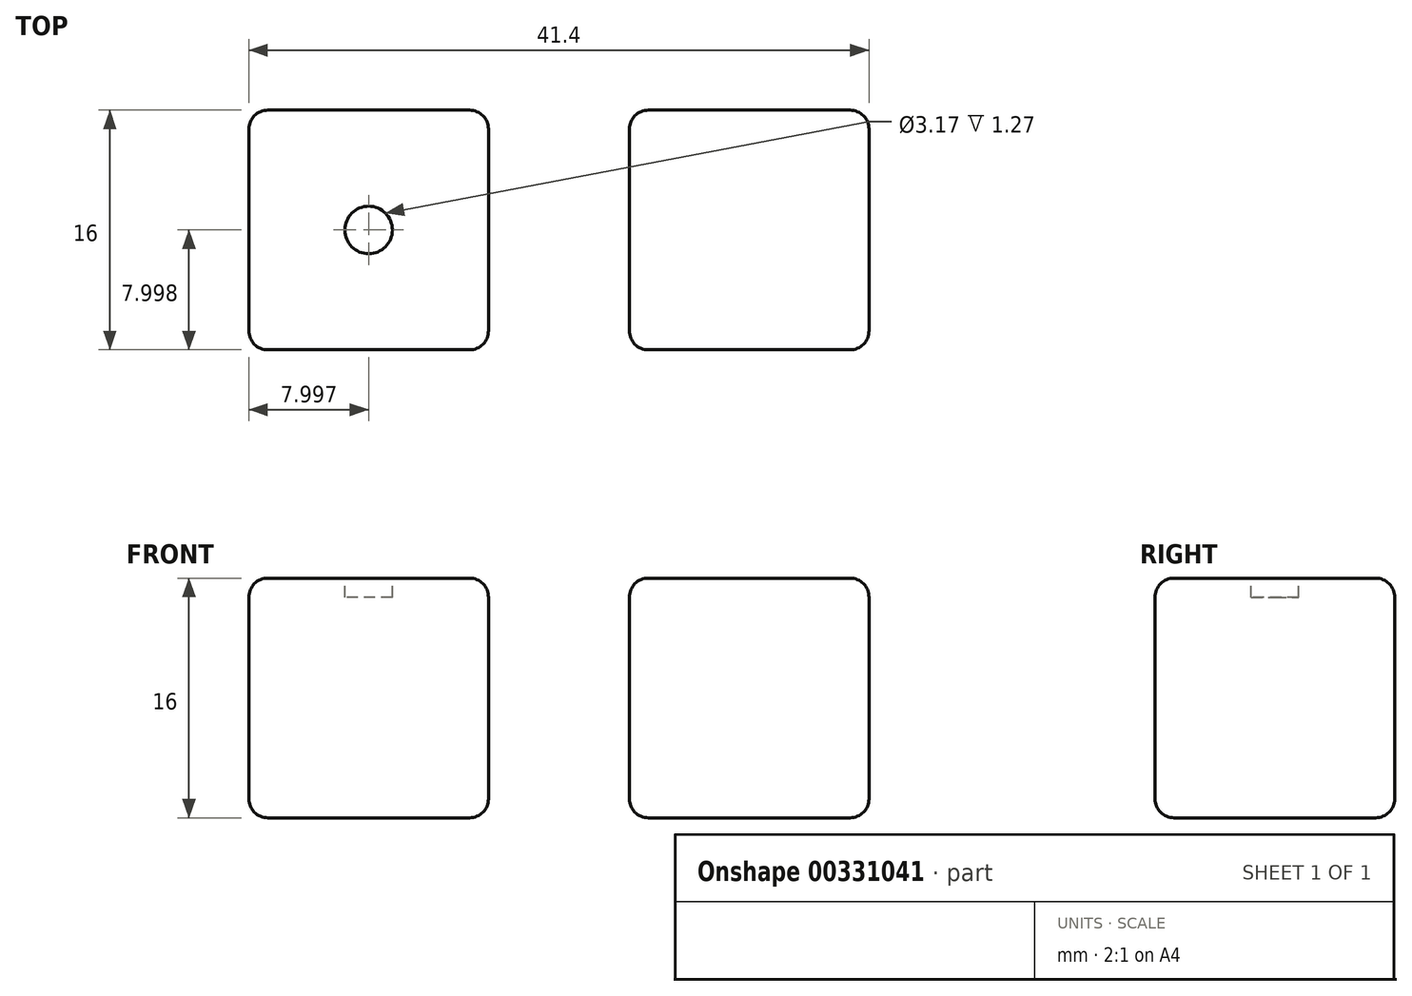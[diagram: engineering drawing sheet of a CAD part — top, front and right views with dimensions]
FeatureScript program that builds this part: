
annotation { "Feature Type Name" : "Feature", "Feature Type Description" : "" }
export const myFeature = defineFeature(function(context is Context, id is Id, definition is map)
    precondition{}
    {
        {
            assignVariable(context, id + "F0", {"name" : "length", "anyValue" : 16 * mm});
        }
        {
            var Q0;
            Q0=qCreatedBy(makeId("Top.planeOp"),FACE);
            var sketch = newSketch(context, id + "F1", { "sketchPlane" : qUnion([Q0])});
            skLineSegment(sketch, "E0.bottom", {"start": v(-39.15, 14.8) * mm, "end": v(-23.15, 14.8) * mm});
            skLineSegment(sketch, "E0.top", {"start": v(-39.15, -1.2) * mm, "end": v(-23.15, -1.2) * mm});
            skLineSegment(sketch, "E0.left", {"start": v(-39.15, 14.8) * mm, "end": v(-39.15, -1.2) * mm});
            skLineSegment(sketch, "E0.right", {"start": v(-23.15, 14.8) * mm, "end": v(-23.15, -1.2) * mm});
            skLineSegment(sketch, "E1.1.0.0", {"start": v(2.25, 14.8) * mm, "end": v(2.25, -1.2) * mm});
            skLineSegment(sketch, "E1.1.0.1", {"start": v(-13.75, 14.8) * mm, "end": v(-13.75, -1.2) * mm});
            skLineSegment(sketch, "E1.1.0.2", {"start": v(-13.75, -1.2) * mm, "end": v(2.25, -1.2) * mm});
            skLineSegment(sketch, "E1.1.0.3", {"start": v(-13.75, 14.8) * mm, "end": v(2.25, 14.8) * mm});
            skLineSegment(sketch, "E1.direction1", {"start": v(-39.15, -1.2) * mm, "end": v(-13.75, -1.2) * mm, "construction": true});
            skSolve(sketch);
        }
        {
            var Q0;
            Q0 = qSketchRegion(id + "F1", true);
            extrude(context, id + "F2", {"entities" : qUnion([Q0]), "depth" : getVariable(context, 'length'), "offsetDistance" : 25.4 * mm});
        }
        {
            var Q0;
            Q0=makeQuery(id+"F2.opExtrude","CAP_EDGE",EDGE,{"disambiguationData":[OSD([sQuery(id+"F1.wireOp",EDGE,"E0.right")])],"isStart":true});
            var Q1;
            Q1=makeQuery(id+"F2.opExtrude","CAP_EDGE",EDGE,{"disambiguationData":[OSD([sQuery(id+"F1.wireOp",EDGE,"E0.left")])],"isStart":false});
            var Q2;
            Q2=makeQuery(id+"F2.opExtrude","CAP_EDGE",EDGE,{"disambiguationData":[OSD([sQuery(id+"F1.wireOp",EDGE,"E0.top")])],"isStart":false});
            var Q3;
            Q3=makeQuery(id+"F2.opExtrude","SWEPT_EDGE",EDGE,{"disambiguationData":[OSD([sQuery(id+"F1.wireOp",EDGE,"E0.bottom"),sQuery(id+"F1.wireOp",EDGE,"E0.right")])]});
            var Q4;
            Q4=makeQuery(id+"F2.opExtrude","SWEPT_EDGE",EDGE,{"disambiguationData":[OSD([sQuery(id+"F1.wireOp",EDGE,"E0.top"),sQuery(id+"F1.wireOp",EDGE,"E0.right")])]});
            var Q5;
            Q5=makeQuery(id+"F2.opExtrude","CAP_EDGE",EDGE,{"disambiguationData":[OSD([sQuery(id+"F1.wireOp",EDGE,"E0.bottom")])],"isStart":false});
            var Q6;
            Q6=makeQuery(id+"F2.opExtrude","SWEPT_EDGE",EDGE,{"disambiguationData":[OSD([sQuery(id+"F1.wireOp",EDGE,"E0.top"),sQuery(id+"F1.wireOp",EDGE,"E0.left")])]});
            var Q7;
            Q7=makeQuery(id+"F2.opExtrude","CAP_EDGE",EDGE,{"disambiguationData":[OSD([sQuery(id+"F1.wireOp",EDGE,"E0.right")])],"isStart":false});
            var Q8;
            Q8=makeQuery(id+"F2.opExtrude","CAP_EDGE",EDGE,{"disambiguationData":[OSD([sQuery(id+"F1.wireOp",EDGE,"E0.top")])],"isStart":true});
            var Q9;
            Q9=makeQuery(id+"F2.opExtrude","CAP_EDGE",EDGE,{"disambiguationData":[OSD([sQuery(id+"F1.wireOp",EDGE,"E1.1.0.2")])],"isStart":true});
            var Q10;
            Q10=makeQuery(id+"F2.opExtrude","CAP_EDGE",EDGE,{"disambiguationData":[OSD([sQuery(id+"F1.wireOp",EDGE,"E1.1.0.0")])],"isStart":true});
            var Q11;
            Q11=makeQuery(id+"F2.opExtrude","SWEPT_EDGE",EDGE,{"disambiguationData":[OSD([sQuery(id+"F1.wireOp",EDGE,"E1.1.0.1"),sQuery(id+"F1.wireOp",EDGE,"E1.1.0.2")])]});
            var Q12;
            Q12=makeQuery(id+"F2.opExtrude","CAP_EDGE",EDGE,{"disambiguationData":[OSD([sQuery(id+"F1.wireOp",EDGE,"E1.1.0.2")])],"isStart":false});
            var Q13;
            Q13=makeQuery(id+"F2.opExtrude","SWEPT_EDGE",EDGE,{"disambiguationData":[OSD([sQuery(id+"F1.wireOp",EDGE,"E1.1.0.0"),sQuery(id+"F1.wireOp",EDGE,"E1.1.0.2")])]});
            var Q14;
            Q14=makeQuery(id+"F2.opExtrude","SWEPT_EDGE",EDGE,{"disambiguationData":[OSD([sQuery(id+"F1.wireOp",EDGE,"E1.1.0.0"),sQuery(id+"F1.wireOp",EDGE,"E1.1.0.3")])]});
            var Q15;
            Q15=makeQuery(id+"F2.opExtrude","CAP_EDGE",EDGE,{"disambiguationData":[OSD([sQuery(id+"F1.wireOp",EDGE,"E1.1.0.1")])],"isStart":false});
            var Q16;
            Q16=makeQuery(id+"F2.opExtrude","CAP_EDGE",EDGE,{"disambiguationData":[OSD([sQuery(id+"F1.wireOp",EDGE,"E1.1.0.3")])],"isStart":false});
            var Q17;
            Q17=makeQuery(id+"F2.opExtrude","CAP_EDGE",EDGE,{"disambiguationData":[OSD([sQuery(id+"F1.wireOp",EDGE,"E1.1.0.0")])],"isStart":false});
            var Q18;
            Q18=makeQuery(id+"F2.opExtrude","SWEPT_EDGE",EDGE,{"disambiguationData":[OSD([sQuery(id+"F1.wireOp",EDGE,"E0.bottom"),sQuery(id+"F1.wireOp",EDGE,"E0.left")])]});
            var Q19;
            Q19=makeQuery(id+"F2.opExtrude","CAP_EDGE",EDGE,{"disambiguationData":[OSD([sQuery(id+"F1.wireOp",EDGE,"E0.left")])],"isStart":true});
            var Q20;
            Q20=makeQuery(id+"F2.opExtrude","CAP_EDGE",EDGE,{"disambiguationData":[OSD([sQuery(id+"F1.wireOp",EDGE,"E0.bottom")])],"isStart":true});
            var Q21;
            Q21=makeQuery(id+"F2.opExtrude","CAP_EDGE",EDGE,{"disambiguationData":[OSD([sQuery(id+"F1.wireOp",EDGE,"E1.1.0.1")])],"isStart":true});
            var Q22;
            Q22=makeQuery(id+"F2.opExtrude","CAP_EDGE",EDGE,{"disambiguationData":[OSD([sQuery(id+"F1.wireOp",EDGE,"E1.1.0.3")])],"isStart":true});
            var Q23;
            Q23=makeQuery(id+"F2.opExtrude","SWEPT_EDGE",EDGE,{"disambiguationData":[OSD([sQuery(id+"F1.wireOp",EDGE,"E1.1.0.1"),sQuery(id+"F1.wireOp",EDGE,"E1.1.0.3")])]});
            fillet(context, id + "F3", {"entities" : qUnion([Q0, Q1, Q2, Q3, Q4, Q5, Q6, Q7, Q8, Q9, Q10, Q11, Q12, Q13, Q14, Q15, Q16, Q17, Q18, Q19, Q20, Q21, Q22, Q23]), "radius" : 1.27 * mm, "tangentPropagation" : true, "allowEdgeOverflow" : false});
        }
        {
            var Q0;
            Q0=makeQuery(id+"F2.opExtrude","CAP_FACE",FACE,{"disambiguationData":[OSD([sQuery(id+"F1.wireOp",EDGE,"E0.bottom"),sQuery(id+"F1.wireOp",EDGE,"E0.top"),sQuery(id+"F1.wireOp",EDGE,"E0.left"),sQuery(id+"F1.wireOp",EDGE,"E0.right")])],"isStart":false});
            var sketch = newSketch(context, id + "F4", { "sketchPlane" : qUnion([Q0])});
            skCircle(sketch, "E2", {"center": v(-31.15, 6.8) * mm, "radius": 1.59 * mm});
            skPoint(sketch, "E2.centerSnap0", {"position": v(-31.15, 13.54) * mm});
            skPoint(sketch, "E2.centerSnap1", {"position": v(-37.88, 6.8) * mm});
            skSolve(sketch);
        }
        {
            var Q0;
            Q0=makeQuery(id+"F4.imprint","IMPRINT",FACE,{"disambiguationData":[TD([[makeQuery(id+"F4.imprint","IMPRINT",EDGE,{"derivedFrom":sQuery(id+"F4.wireOp",EDGE,"E2")}),1.0]])]});
            extrude(context, id + "F5", {"entities" : qUnion([Q0]), "operationType" : NewBodyOperationType.REMOVE, "oppositeDirection" : true, "depth" : 1.27 * mm, "offsetDistance" : 25.4 * mm});
        }
    });
